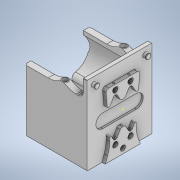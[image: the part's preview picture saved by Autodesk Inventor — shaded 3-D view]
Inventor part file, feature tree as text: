
AUTODESK INVENTOR PART (.ipt)
format: ipt  version: 2022 (Build 260153000, 153)  size: 997,376 bytes
history: native  units: mm
features: sketch x21, reference x20, projected_geometry x20, extrude x19, fillet x11, other x7, chamfer x1
ambient origin geometry x8: Origin, YZ Plane, XZ Plane, XY Plane, X Axis, Y Axis, Z Axis, Center Point
bodies: Body1 (feature_tree)
feature tree (99):
  other  "Твердое тело1"
  extrude  "Выдавливание1"  Depth=34.5mm TaperAngle=0.0deg
  extrude  "Выдавливание2"  Depth=0.5mm
  extrude  "Выдавливание3"  Depth=0.3mm
  extrude  "Выдавливание4"  Depth=5.0mm
  extrude  "Выдавливание5"  Depth=5.0mm
  extrude  "Выдавливание6"  Depth=5.0mm
  extrude  "Выдавливание8"  Depth=15.0mm
  extrude  "Выдавливание9"  Depth=15.0mm
  chamfer  "Фаска1"  Distance=15.0mm
  fillet  "Сопряжение1"  Radius=1.7mm
  extrude  "Выдавливание11"  Depth=2.0mm TaperAngle=0.0deg
  fillet  "Сопряжение4"  Radius=0.8mm
  fillet  "Сопряжение5"  Radius=4.7mm
  sketch  "Эскиз15"
  extrude  "Выдавливание12"  Depth=0.4mm
  sketch  "Эскиз17"
  extrude  "Выдавливание13"  Depth=0.4mm
  fillet  "Сопряжение6"  Radius=200.0mm
  fillet  "Сопряжение7"  Radius=0.5mm
  fillet  "Сопряжение8"  Radius=2.3mm
  fillet  "Сопряжение9"  Radius=10.0mm
  extrude  "Выдавливание14"  Depth=10.0mm
  fillet  "Сопряжение10"  Radius=3.0mm
  extrude  "Выдавливание15"  Depth=4.0mm
  extrude  "Выдавливание16"  Depth=3.0mm
  extrude  "Выдавливание17"  Depth=4.0mm
  fillet  "Сопряжение11"  Radius=2.3mm
  fillet  "Сопряжение12"  Radius=2.3mm
  extrude  "Выдавливание18"  Depth=10.0mm
  extrude  "Выдавливание19"  Depth=30.0mm
  extrude  "Выдавливание20"  Depth=0.8mm TaperAngle=0.0deg
  extrude  "Выдавливание21"  Depth=0.15mm
  fillet  "Сопряжение13"  Radius=3.0mm
  sketch  "Эскиз1"
  reference  "Ссылка1"
  reference  "Ссылка2"
  reference  "Ссылка3"
  reference  "Ссылка4"
  reference  "Ссылка5"
  reference  "Ссылка6"
  reference  "Ссылка7"
  reference  "Ссылка8"
  sketch  "Эскиз2"
  projected_geometry  "Спроецированная петля1"
  projected_geometry  "Спроецированная петля2"
  sketch  "Эскиз3"
  reference  "Ссылка9"
  reference  "Ссылка10"
  sketch  "Эскиз4"
  projected_geometry  "Спроецированная петля3"
  reference  "Ссылка11"
  reference  "Ссылка12"
  reference  "Ссылка13"
  reference  "Ссылка14"
  sketch  "Эскиз5"
  reference  "Ссылка15"
  reference  "Ссылка16"
  projected_geometry  "Спроецированная петля4"
  sketch  "Эскиз7"
  projected_geometry  "Спроецированная петля6"
  sketch  "Эскиз11"
  projected_geometry  "Спроецированная петля8"
  sketch  "Эскиз12"
  reference  "Ссылка27"
  sketch  "Эскиз14"
  sketch  "Эскиз16"
  reference  "Ссылка29"
  projected_geometry  "Спроецированная петля10"
  projected_geometry  "Спроецированная петля11"
  projected_geometry  "Спроецированная петля12"
  reference  "Ссылка30"
  reference  "Ссылка31"
  sketch  "Эскиз18"
  projected_geometry  "Спроецированная петля14"
  sketch  "Эскиз19"
  projected_geometry  "Спроецированная петля15"
  projected_geometry  "Спроецированная петля16"
  sketch  "Эскиз20"
  projected_geometry  "Спроецированная петля17"
  projected_geometry  "Спроецированная петля18"
  sketch  "Эскиз21"
  projected_geometry  "Спроецированная петля19"
  projected_geometry  "Спроецированная петля20"
  projected_geometry  "Спроецированная петля21"
  projected_geometry  "Спроецированная петля22"
  sketch  "Эскиз22"
  sketch  "Эскиз23"
  projected_geometry  "Спроецированная петля23"
  sketch  "Эскиз24"
  projected_geometry  "Спроецированная петля24"
  sketch  "Эскиз25"
  sketch  "Эскиз26"
  other  "<userpath>\OneDrive\Документы\Git\MZCAT_battery\FastBattery.iam"
  other  "FastBattery.iam"
  other  "plan:1"
  other  "BMS_board:1"
  other  "metal_body:1"
  other  "metal_cap:1"
